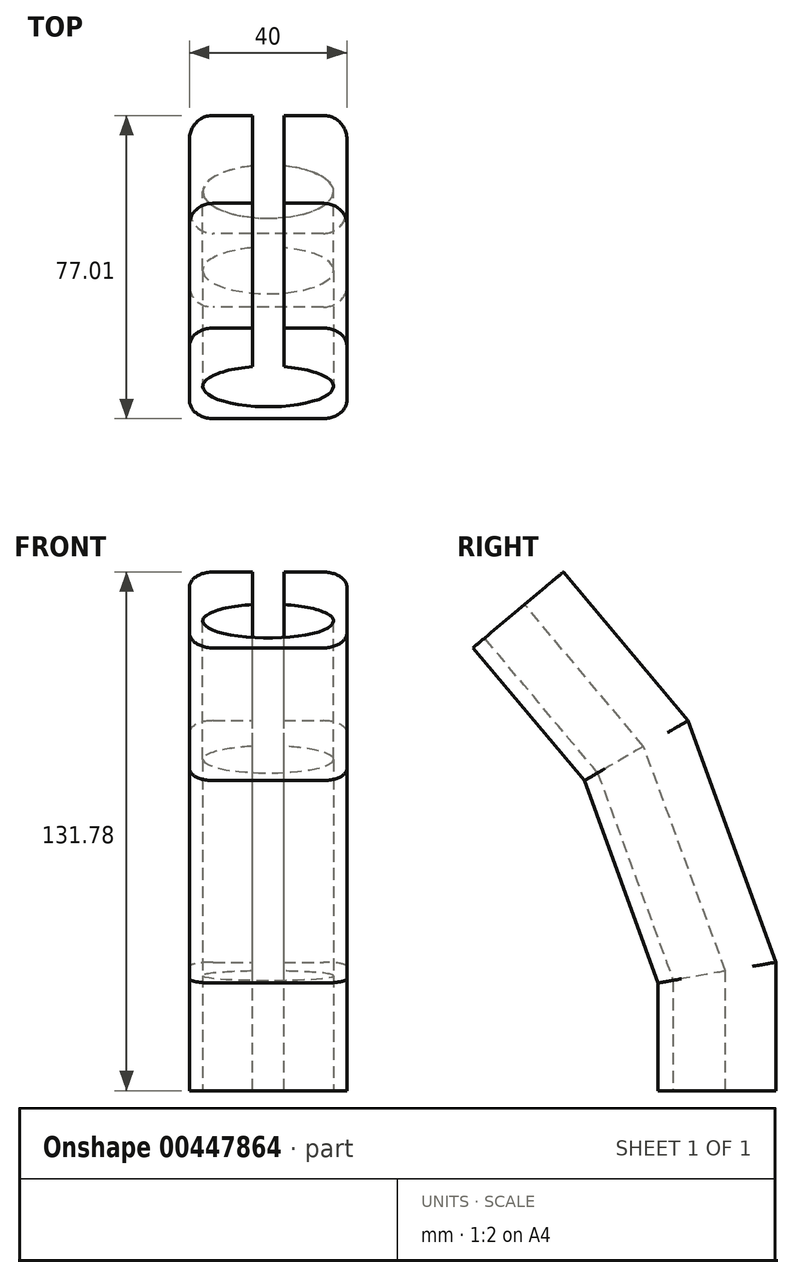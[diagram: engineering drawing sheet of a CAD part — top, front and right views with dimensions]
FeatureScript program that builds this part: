
annotation { "Feature Type Name" : "Feature", "Feature Type Description" : "" }
export const myFeature = defineFeature(function(context is Context, id is Id, definition is map)
    precondition{}
    {
        {
            var Q0;
            Q0=qCreatedBy(makeId("Top.planeOp"),FACE);
            var sketch = newSketch(context, id + "F0", { "sketchPlane" : qUnion([Q0])});
            skLineSegment(sketch, "E0.bottom", {"start": v(14, -15) * mm, "end": v(-14, -15) * mm});
            skLineSegment(sketch, "E0.top", {"start": v(14, 15) * mm, "end": v(4, 15) * mm});
            skLineSegment(sketch, "E0.left", {"start": v(20, -9) * mm, "end": v(20, 9) * mm});
            skLineSegment(sketch, "E0.right", {"start": v(-20, -9) * mm, "end": v(-20, 9) * mm});
            skPoint(sketch, "E0.middle", {"position": v(0, 0) * mm});
            skPoint(sketch, "E1", {"position": v(-4, 15) * mm});
            skPoint(sketch, "E2", {"position": v(4, 15) * mm});
            skLineSegment(sketch, "E3.trimOffspring", {"start": v(-4, 15) * mm, "end": v(-14, 15) * mm});
            skEllipticalArc(sketch, "E4", {});
            skLineSegment(sketch, "E5", {"start": v(4, 15) * mm, "end": v(4, 2.16) * mm});
            skLineSegment(sketch, "E6", {"start": v(-4, 15) * mm, "end": v(-4, 2.16) * mm});
            skPoint(sketch, "E7", {"position": v(-14, 15) * mm});
            skPoint(sketch, "E8", {"position": v(-20, 9) * mm});
            skArc(sketch, "E9", {"start": v(-14, 15) * mm, "mid": v(-18.24, 13.24) * mm, "end": v(-20, 9) * mm});
            skArc(sketch, "E10.MirrorCS", {"start": v(-14, -15) * mm, "mid": v(-18.24, -13.24) * mm, "end": v(-20, -9) * mm});
            skArc(sketch, "E11.MirrorCS", {"start": v(14, 15) * mm, "mid": v(18.24, 13.24) * mm, "end": v(20, 9) * mm});
            skArc(sketch, "E12.MirrorCS", {"start": v(14, -15) * mm, "mid": v(18.24, -13.24) * mm, "end": v(20, -9) * mm});
            const initialGuessF0  = {"E4": [0, -0.004381569102406502, -1, 0, 0.0166404377669096, 0.006738508382452839, 4.9551445309350655, 4.469633429834314]};
            skSetInitialGuess(sketch, initialGuessF0);
            skSolve(sketch);
        }
        {
            var Q0;
            Q0=qCreatedBy(makeId("Right.planeOp"),FACE);
            var sketch = newSketch(context, id + "F1", { "sketchPlane" : qUnion([Q0])});
            skLineSegment(sketch, "E13", {"start": v(0, 0) * mm, "end": v(0, 30) * mm});
            skLineSegment(sketch, "E14", {"start": v(0, 30) * mm, "end": v(-20.52, 86.38) * mm});
            skLineSegment(sketch, "E15", {"start": v(-20.52, 86.38) * mm, "end": v(-50.52, 122.13) * mm});
            skSolve(sketch);
        }
        {
            var Q0;
            Q0=makeQuery(id+"F0.imprint","IMPRINT",FACE,{"disambiguationData":[TD([[makeQuery(id+"F0.imprint","IMPRINT",EDGE,{"derivedFrom":sQuery(id+"F0.wireOp",EDGE,"E0.bottom")}),-1.0]])]});
            var Q1;
            Q1 = qConstructionFilter(qBodyType(qCreatedBy(id + "F1" ,EDGE), BodyType.WIRE), ConstructionObject.NO);
            sweep(context, id + "F2", {"profiles" : qUnion([Q0]), "path" : qUnion([Q1])});
        }
    });
